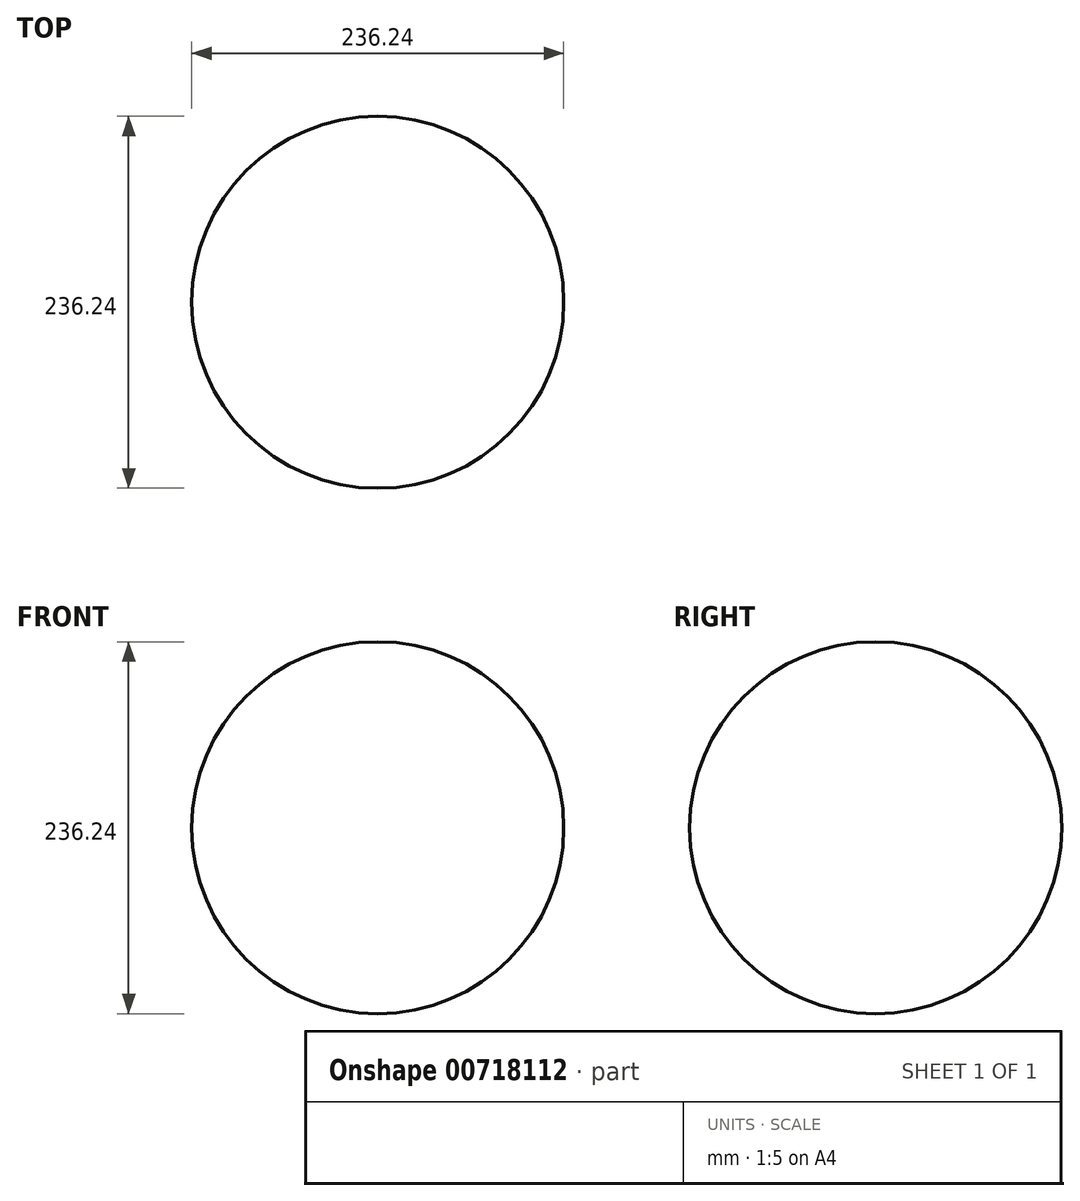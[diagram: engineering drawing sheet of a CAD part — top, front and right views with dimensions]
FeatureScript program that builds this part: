
annotation { "Feature Type Name" : "Feature", "Feature Type Description" : "" }
export const myFeature = defineFeature(function(context is Context, id is Id, definition is map)
    precondition{}
    {
        {
            var Q0;
            Q0=qCreatedBy(makeId("Top.planeOp"),FACE);
            var sketch = newSketch(context, id + "F0", { "sketchPlane" : qUnion([Q0])});
            skCircle(sketch, "E0", {"center": v(0, 0) * mm, "radius": 118.12 * mm});
            skLineSegment(sketch, "E1", {"start": v(0, 118.12) * mm, "end": v(0, -118.12) * mm});
            skSolve(sketch);
        }
        {
            var Q0;
            {var subQ0=sQuery(id+"F0.wireOp",EDGE,"E1");Q0=makeQuery(id+"F0.imprint","IMPRINT",FACE,{"disambiguationData":[TD([[makeQuery(id+"F0.imprint","IMPRINT",EDGE,{"derivedFrom":subQ0}),1.0]])]});}
            var Q1;
            Q1=sQuery(id+"F0.wireOp",EDGE,"E1");
            revolve(context, id + "F1", {"surfaceOperationType" : NewSurfaceOperationType.NEW, "entities" : qUnion([Q0]), "axis" : qUnion([Q1]), "revolveType" : RevolveType.FULL});
        }
    });
